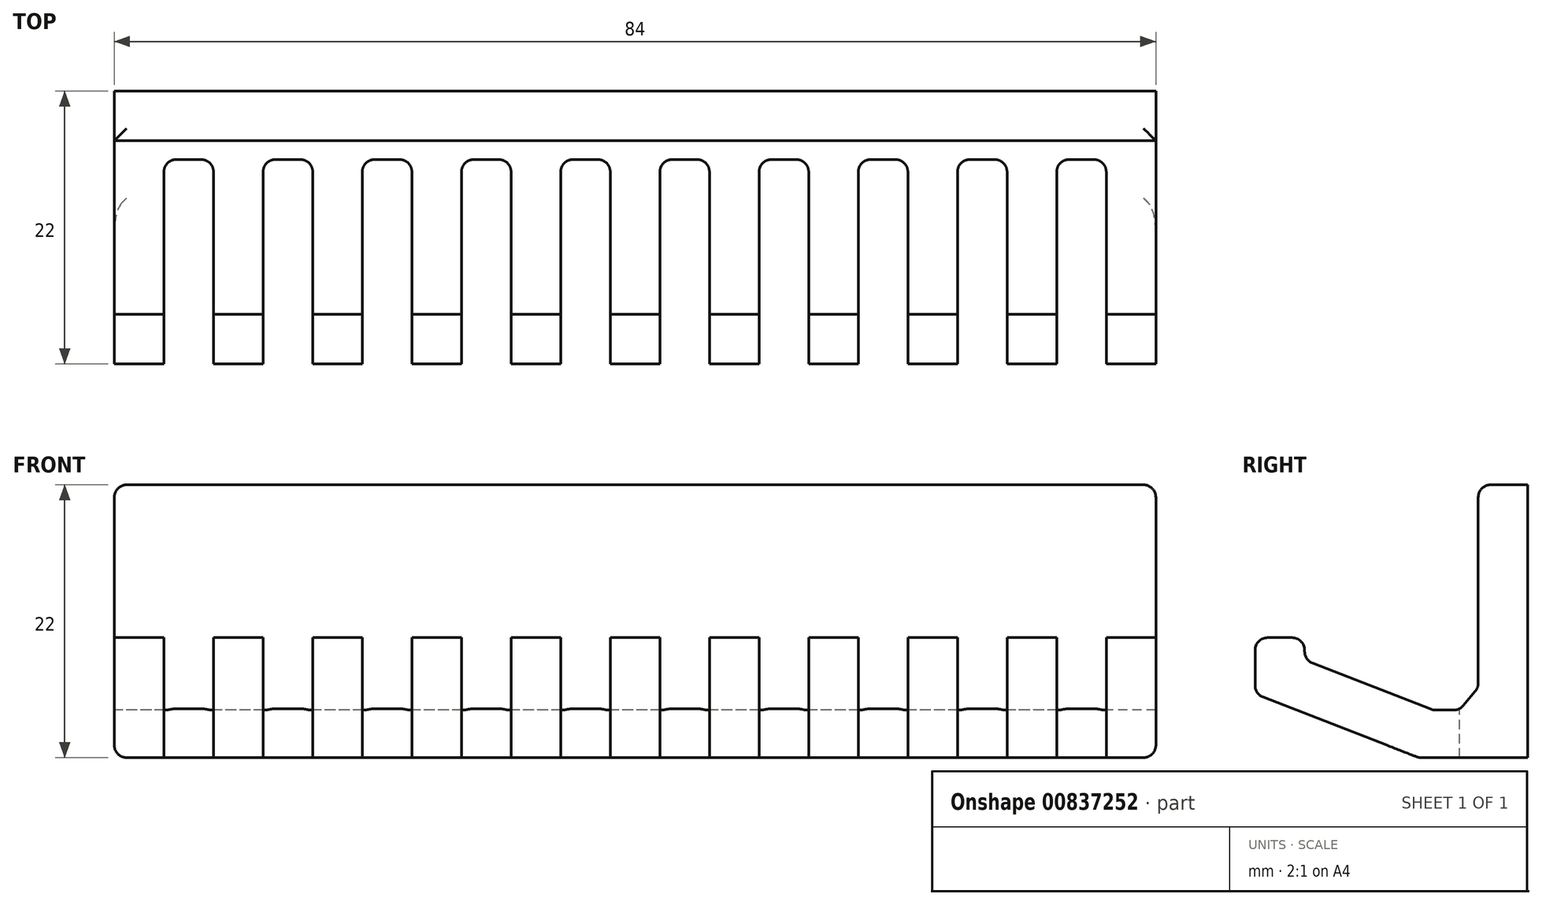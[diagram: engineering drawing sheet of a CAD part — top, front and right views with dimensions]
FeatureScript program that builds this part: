
annotation { "Feature Type Name" : "Feature", "Feature Type Description" : "" }
export const myFeature = defineFeature(function(context is Context, id is Id, definition is map)
    precondition{}
    {
        {
            var Q0;
            Q0=qCreatedBy(makeId("Right.planeOp"),FACE);
            var sketch = newSketch(context, id + "F0", { "sketchPlane" : qUnion([Q0])});
            skLineSegment(sketch, "E0", {"start": v(0, 0) * mm, "end": v(0, 22) * mm});
            skLineSegment(sketch, "E1", {"start": v(0, 22) * mm, "end": v(-4, 22) * mm});
            skLineSegment(sketch, "E2", {"start": v(-4, 22) * mm, "end": v(-4, 5.64) * mm});
            skLineSegment(sketch, "E3", {"start": v(-4, 5.64) * mm, "end": v(-5.52, 3.83) * mm});
            skLineSegment(sketch, "E4", {"start": v(-5.52, 3.83) * mm, "end": v(-7.62, 3.83) * mm});
            skLineSegment(sketch, "E5", {"start": v(-7.62, 3.83) * mm, "end": v(-18, 7.86) * mm});
            skLineSegment(sketch, "E6", {"start": v(-18, 7.86) * mm, "end": v(-18, 9.67) * mm});
            skLineSegment(sketch, "E7", {"start": v(-18, 9.67) * mm, "end": v(-22, 9.67) * mm});
            skLineSegment(sketch, "E8", {"start": v(-22, 9.67) * mm, "end": v(-22, 5.13) * mm});
            skLineSegment(sketch, "E9", {"start": v(-22, 5.13) * mm, "end": v(-8.8, 0) * mm});
            skLineSegment(sketch, "E10", {"start": v(-8.8, 0) * mm, "end": v(0, 0) * mm});
            skSolve(sketch);
        }
        {
            var Q0;
            Q0 = qSketchRegion(id + "F0", true);
            extrude(context, id + "F1", {"entities" : qUnion([Q0]), "depth" : 84 * mm, "offsetDistance" : 25 * mm});
        }
        {
            var Q0;
            Q0=makeQuery(id+"F1.opExtrude","SWEPT_FACE",FACE,{"disambiguationData":[OSD([sQuery(id+"F0.wireOp",EDGE,"E7")])]});
            var sketch = newSketch(context, id + "F2", { "sketchPlane" : qUnion([Q0])});
            skLineSegment(sketch, "E11.bottom", {"start": v(4, -22) * mm, "end": v(8, -22) * mm});
            skLineSegment(sketch, "E11.top", {"start": v(5, -5.52) * mm, "end": v(7, -5.52) * mm});
            skLineSegment(sketch, "E11.left", {"start": v(4, -22) * mm, "end": v(4, -6.52) * mm});
            skLineSegment(sketch, "E11.right", {"start": v(8, -22) * mm, "end": v(8, -6.52) * mm});
            skLineSegment(sketch, "E12.1.0.0", {"start": v(12, -22) * mm, "end": v(16, -22) * mm});
            skLineSegment(sketch, "E12.1.0.1", {"start": v(12, -22) * mm, "end": v(12, -6.52) * mm});
            skLineSegment(sketch, "E12.1.0.2", {"start": v(13, -5.52) * mm, "end": v(15, -5.52) * mm});
            skLineSegment(sketch, "E12.1.0.3", {"start": v(16, -22) * mm, "end": v(16, -6.52) * mm});
            skLineSegment(sketch, "E12.2.0.0", {"start": v(20, -22) * mm, "end": v(24, -22) * mm});
            skLineSegment(sketch, "E12.2.0.1", {"start": v(20, -22) * mm, "end": v(20, -6.52) * mm});
            skLineSegment(sketch, "E12.2.0.2", {"start": v(21, -5.52) * mm, "end": v(23, -5.52) * mm});
            skLineSegment(sketch, "E12.2.0.3", {"start": v(24, -22) * mm, "end": v(24, -6.52) * mm});
            skLineSegment(sketch, "E12.3.0.0", {"start": v(28, -22) * mm, "end": v(32, -22) * mm});
            skLineSegment(sketch, "E12.3.0.1", {"start": v(28, -22) * mm, "end": v(28, -6.52) * mm});
            skLineSegment(sketch, "E12.3.0.2", {"start": v(29, -5.52) * mm, "end": v(31, -5.52) * mm});
            skLineSegment(sketch, "E12.3.0.3", {"start": v(32, -22) * mm, "end": v(32, -6.52) * mm});
            skLineSegment(sketch, "E12.4.0.0", {"start": v(36, -22) * mm, "end": v(40, -22) * mm});
            skLineSegment(sketch, "E12.4.0.1", {"start": v(36, -22) * mm, "end": v(36, -6.52) * mm});
            skLineSegment(sketch, "E12.4.0.2", {"start": v(37, -5.52) * mm, "end": v(39, -5.52) * mm});
            skLineSegment(sketch, "E12.4.0.3", {"start": v(40, -22) * mm, "end": v(40, -6.52) * mm});
            skLineSegment(sketch, "E12.5.0.0", {"start": v(44, -22) * mm, "end": v(48, -22) * mm});
            skLineSegment(sketch, "E12.5.0.1", {"start": v(44, -22) * mm, "end": v(44, -6.52) * mm});
            skLineSegment(sketch, "E12.5.0.2", {"start": v(45, -5.52) * mm, "end": v(47, -5.52) * mm});
            skLineSegment(sketch, "E12.5.0.3", {"start": v(48, -22) * mm, "end": v(48, -6.52) * mm});
            skLineSegment(sketch, "E12.6.0.0", {"start": v(52, -22) * mm, "end": v(56, -22) * mm});
            skLineSegment(sketch, "E12.6.0.1", {"start": v(52, -22) * mm, "end": v(52, -6.52) * mm});
            skLineSegment(sketch, "E12.6.0.2", {"start": v(53, -5.52) * mm, "end": v(55, -5.52) * mm});
            skLineSegment(sketch, "E12.6.0.3", {"start": v(56, -22) * mm, "end": v(56, -6.52) * mm});
            skLineSegment(sketch, "E12.7.0.0", {"start": v(60, -22) * mm, "end": v(64, -22) * mm});
            skLineSegment(sketch, "E12.7.0.1", {"start": v(60, -22) * mm, "end": v(60, -6.52) * mm});
            skLineSegment(sketch, "E12.7.0.2", {"start": v(61, -5.52) * mm, "end": v(63, -5.52) * mm});
            skLineSegment(sketch, "E12.7.0.3", {"start": v(64, -22) * mm, "end": v(64, -6.52) * mm});
            skLineSegment(sketch, "E12.8.0.0", {"start": v(68, -22) * mm, "end": v(72, -22) * mm});
            skLineSegment(sketch, "E12.8.0.1", {"start": v(68, -22) * mm, "end": v(68, -6.52) * mm});
            skLineSegment(sketch, "E12.8.0.2", {"start": v(69, -5.52) * mm, "end": v(71, -5.52) * mm});
            skLineSegment(sketch, "E12.8.0.3", {"start": v(72, -22) * mm, "end": v(72, -6.52) * mm});
            skLineSegment(sketch, "E12.9.0.0", {"start": v(76, -22) * mm, "end": v(80, -22) * mm});
            skLineSegment(sketch, "E12.9.0.1", {"start": v(76, -22) * mm, "end": v(76, -6.52) * mm});
            skLineSegment(sketch, "E12.9.0.2", {"start": v(77, -5.52) * mm, "end": v(79, -5.52) * mm});
            skLineSegment(sketch, "E12.9.0.3", {"start": v(80, -22) * mm, "end": v(80, -6.52) * mm});
            skLineSegment(sketch, "E12.direction1", {"start": v(4, -22) * mm, "end": v(12, -22) * mm, "construction": true});
            skPoint(sketch, "E13.visualSharp", {"position": v(4, -5.52) * mm});
            skArc(sketch, "E13.filletArc", {"start": v(5, -5.52) * mm, "mid": v(4.3, -5.81) * mm, "end": v(4, -6.52) * mm});
            skPoint(sketch, "E14.visualSharp", {"position": v(8, -5.52) * mm});
            skArc(sketch, "E14.filletArc", {"start": v(8, -6.52) * mm, "mid": v(7.7, -5.81) * mm, "end": v(7, -5.52) * mm});
            skPoint(sketch, "E15.visualSharp", {"position": v(12, -5.52) * mm});
            skArc(sketch, "E15.filletArc", {"start": v(13, -5.52) * mm, "mid": v(12.3, -5.81) * mm, "end": v(12, -6.52) * mm});
            skPoint(sketch, "E16.visualSharp", {"position": v(16, -5.52) * mm});
            skArc(sketch, "E16.filletArc", {"start": v(16, -6.52) * mm, "mid": v(15.7, -5.81) * mm, "end": v(15, -5.52) * mm});
            skPoint(sketch, "E17.visualSharp", {"position": v(20, -5.52) * mm});
            skArc(sketch, "E17.filletArc", {"start": v(21, -5.52) * mm, "mid": v(20.3, -5.81) * mm, "end": v(20, -6.52) * mm});
            skPoint(sketch, "E18.visualSharp", {"position": v(24, -5.52) * mm});
            skArc(sketch, "E18.filletArc", {"start": v(24, -6.52) * mm, "mid": v(23.7, -5.81) * mm, "end": v(23, -5.52) * mm});
            skPoint(sketch, "E19.visualSharp", {"position": v(28, -5.52) * mm});
            skArc(sketch, "E19.filletArc", {"start": v(29, -5.52) * mm, "mid": v(28.3, -5.81) * mm, "end": v(28, -6.52) * mm});
            skPoint(sketch, "E20.visualSharp", {"position": v(32, -5.52) * mm});
            skArc(sketch, "E20.filletArc", {"start": v(32, -6.52) * mm, "mid": v(31.7, -5.81) * mm, "end": v(31, -5.52) * mm});
            skPoint(sketch, "E21.visualSharp", {"position": v(36, -5.52) * mm});
            skArc(sketch, "E21.filletArc", {"start": v(37, -5.52) * mm, "mid": v(36.3, -5.81) * mm, "end": v(36, -6.52) * mm});
            skPoint(sketch, "E22.visualSharp", {"position": v(40, -5.52) * mm});
            skArc(sketch, "E22.filletArc", {"start": v(40, -6.52) * mm, "mid": v(39.7, -5.81) * mm, "end": v(39, -5.52) * mm});
            skPoint(sketch, "E23.visualSharp", {"position": v(44, -5.52) * mm});
            skArc(sketch, "E23.filletArc", {"start": v(45, -5.52) * mm, "mid": v(44.3, -5.81) * mm, "end": v(44, -6.52) * mm});
            skPoint(sketch, "E24.visualSharp", {"position": v(48, -5.52) * mm});
            skArc(sketch, "E24.filletArc", {"start": v(48, -6.52) * mm, "mid": v(47.7, -5.81) * mm, "end": v(47, -5.52) * mm});
            skPoint(sketch, "E25.visualSharp", {"position": v(52, -5.52) * mm});
            skArc(sketch, "E25.filletArc", {"start": v(53, -5.52) * mm, "mid": v(52.3, -5.81) * mm, "end": v(52, -6.52) * mm});
            skPoint(sketch, "E26.visualSharp", {"position": v(56, -5.52) * mm});
            skArc(sketch, "E26.filletArc", {"start": v(56, -6.52) * mm, "mid": v(55.7, -5.81) * mm, "end": v(55, -5.52) * mm});
            skPoint(sketch, "E27.visualSharp", {"position": v(60, -5.52) * mm});
            skArc(sketch, "E27.filletArc", {"start": v(61, -5.52) * mm, "mid": v(60.3, -5.81) * mm, "end": v(60, -6.52) * mm});
            skPoint(sketch, "E28.visualSharp", {"position": v(64, -5.52) * mm});
            skArc(sketch, "E28.filletArc", {"start": v(64, -6.52) * mm, "mid": v(63.7, -5.81) * mm, "end": v(63, -5.52) * mm});
            skPoint(sketch, "E29.visualSharp", {"position": v(68, -5.52) * mm});
            skArc(sketch, "E29.filletArc", {"start": v(69, -5.52) * mm, "mid": v(68.3, -5.81) * mm, "end": v(68, -6.52) * mm});
            skPoint(sketch, "E30.visualSharp", {"position": v(72, -5.52) * mm});
            skArc(sketch, "E30.filletArc", {"start": v(72, -6.52) * mm, "mid": v(71.7, -5.81) * mm, "end": v(71, -5.52) * mm});
            skPoint(sketch, "E31.visualSharp", {"position": v(76, -5.52) * mm});
            skArc(sketch, "E31.filletArc", {"start": v(77, -5.52) * mm, "mid": v(76.3, -5.81) * mm, "end": v(76, -6.52) * mm});
            skPoint(sketch, "E32.visualSharp", {"position": v(80, -5.52) * mm});
            skArc(sketch, "E32.filletArc", {"start": v(80, -6.52) * mm, "mid": v(79.7, -5.81) * mm, "end": v(79, -5.52) * mm});
            skSolve(sketch);
        }
        {
            var Q0;
            Q0=makeQuery(id+"F1.opExtrude","SWEPT_EDGE",EDGE,{"disambiguationData":[OSD([sQuery(id+"F0.wireOp",EDGE,"E7"),sQuery(id+"F0.wireOp",EDGE,"E8")])]});
            var Q1;
            Q1=makeQuery(id+"F1.opExtrude","SWEPT_EDGE",EDGE,{"disambiguationData":[OSD([sQuery(id+"F0.wireOp",EDGE,"E6"),sQuery(id+"F0.wireOp",EDGE,"E7")])]});
            var Q2;
            Q2=makeQuery(id+"F1.opExtrude","SWEPT_EDGE",EDGE,{"disambiguationData":[OSD([sQuery(id+"F0.wireOp",EDGE,"E8"),sQuery(id+"F0.wireOp",EDGE,"E9")])]});
            var Q3;
            Q3=makeQuery(id+"F1.opExtrude","SWEPT_EDGE",EDGE,{"disambiguationData":[OSD([sQuery(id+"F0.wireOp",EDGE,"E5"),sQuery(id+"F0.wireOp",EDGE,"E6")])]});
            var Q4;
            Q4=makeQuery(id+"F1.opExtrude","SWEPT_EDGE",EDGE,{"disambiguationData":[OSD([sQuery(id+"F0.wireOp",EDGE,"E3"),sQuery(id+"F0.wireOp",EDGE,"E4")])]});
            var Q5;
            Q5=makeQuery(id+"F1.opExtrude","SWEPT_EDGE",EDGE,{"disambiguationData":[OSD([sQuery(id+"F0.wireOp",EDGE,"E4"),sQuery(id+"F0.wireOp",EDGE,"E5")])]});
            var Q6;
            Q6=makeQuery(id+"F1.opExtrude","SWEPT_EDGE",EDGE,{"disambiguationData":[OSD([sQuery(id+"F0.wireOp",EDGE,"E2"),sQuery(id+"F0.wireOp",EDGE,"E3")])]});
            var Q7;
            Q7=makeQuery(id+"F1.opExtrude","SWEPT_EDGE",EDGE,{"disambiguationData":[OSD([sQuery(id+"F0.wireOp",EDGE,"E1"),sQuery(id+"F0.wireOp",EDGE,"E2")])]});
            var Q8;
            Q8=makeQuery(id+"F1.opExtrude","CAP_EDGE",EDGE,{"disambiguationData":[OSD([sQuery(id+"F0.wireOp",EDGE,"E1")])],"isStart":true});
            var Q9;
            Q9=makeQuery(id+"F1.opExtrude","CAP_EDGE",EDGE,{"disambiguationData":[OSD([sQuery(id+"F0.wireOp",EDGE,"E1")])],"isStart":false});
            var Q10;
            Q10=makeQuery(id+"F1.opExtrude","CAP_EDGE",EDGE,{"disambiguationData":[OSD([sQuery(id+"F0.wireOp",EDGE,"E10")])],"isStart":true});
            var Q11;
            Q11=makeQuery(id+"F1.opExtrude","CAP_EDGE",EDGE,{"disambiguationData":[OSD([sQuery(id+"F0.wireOp",EDGE,"E10")])],"isStart":false});
            var Q12;
            Q12=makeQuery(id+"F1.opExtrude","SWEPT_EDGE",EDGE,{"disambiguationData":[OSD([sQuery(id+"F0.wireOp",EDGE,"E9"),sQuery(id+"F0.wireOp",EDGE,"E10")])]});
            fillet(context, id + "F3", {"entities" : qUnion([Q0, Q1, Q2, Q3, Q4, Q5, Q6, Q7, Q8, Q9, Q10, Q11, Q12]), "radius" : 1 * mm, "tangentPropagation" : true, "allowEdgeOverflow" : false});
        }
        {
            var Q0;
            Q0 = qSketchRegion(id + "F2", true);
            extrude(context, id + "F4", {"entities" : qUnion([Q0]), "operationType" : NewBodyOperationType.REMOVE, "oppositeDirection" : true, "depth" : 25 * mm, "offsetDistance" : 25 * mm});
        }
    });
